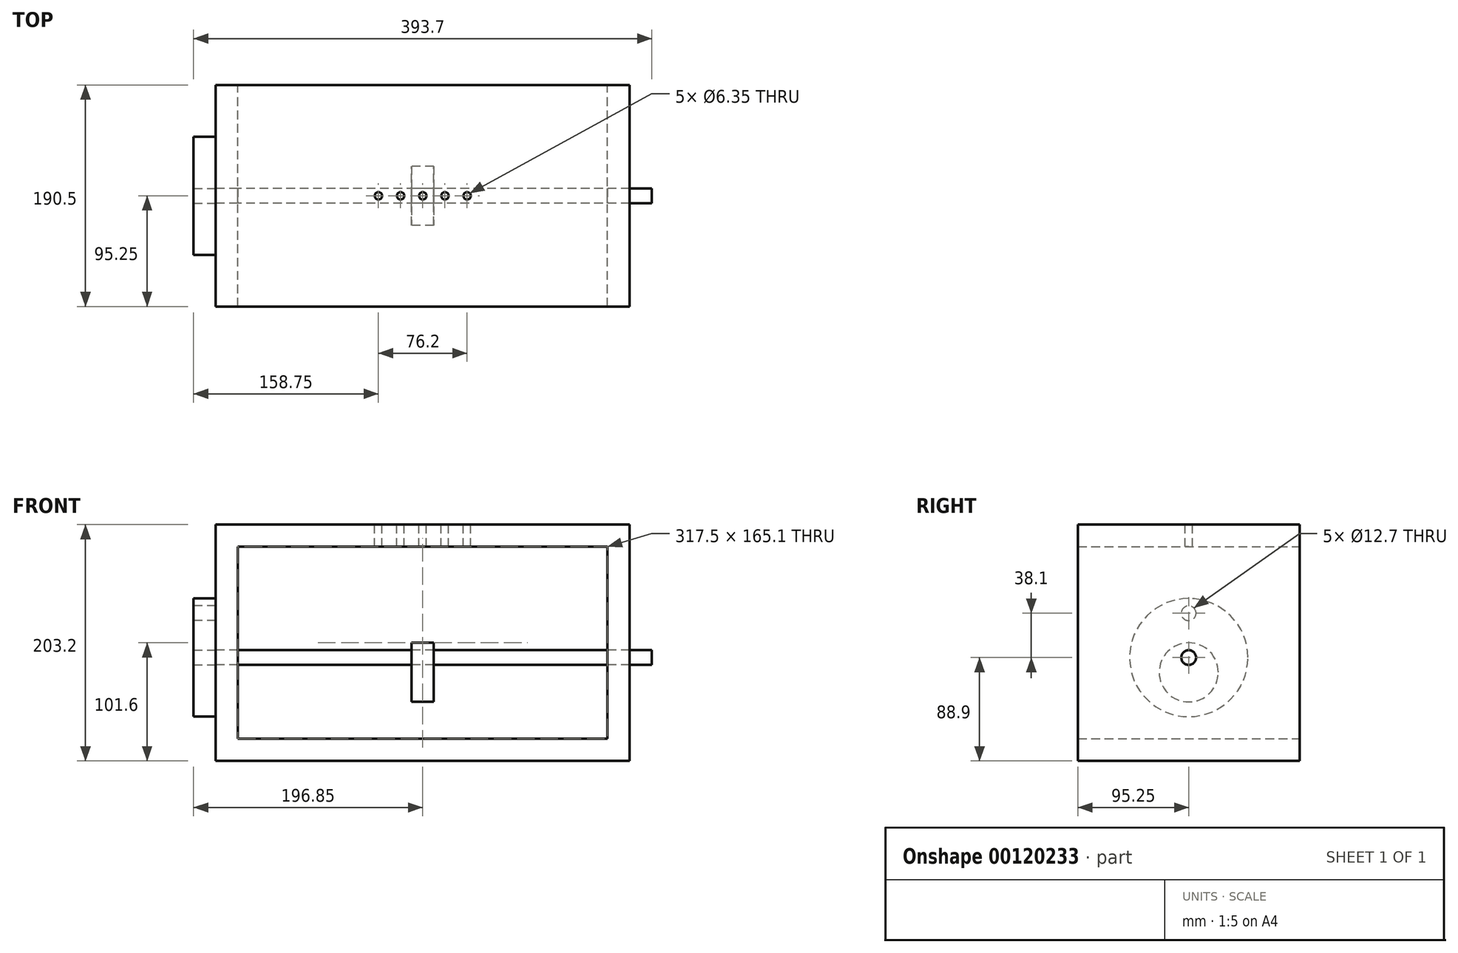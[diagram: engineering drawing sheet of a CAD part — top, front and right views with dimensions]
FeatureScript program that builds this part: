
annotation { "Feature Type Name" : "Feature", "Feature Type Description" : "" }
export const myFeature = defineFeature(function(context is Context, id is Id, definition is map)
    precondition{}
    {
        {
            var Q0;
            Q0=qCreatedBy(makeId("Front.planeOp"),FACE);
            var sketch = newSketch(context, id + "F0", { "sketchPlane" : qUnion([Q0])});
            skLineSegment(sketch, "E0.bottom", {"start": v(158.75, -82.55) * mm, "end": v(-158.75, -82.55) * mm});
            skLineSegment(sketch, "E0.top", {"start": v(158.75, 82.55) * mm, "end": v(-158.75, 82.55) * mm});
            skLineSegment(sketch, "E0.left", {"start": v(158.75, -82.55) * mm, "end": v(158.75, 82.55) * mm});
            skLineSegment(sketch, "E0.right", {"start": v(-158.75, -82.55) * mm, "end": v(-158.75, 82.55) * mm});
            skPoint(sketch, "E0.middle", {"position": v(0, 0) * mm});
            skLineSegment(sketch, "E1.bottom", {"start": v(177.8, -101.6) * mm, "end": v(-177.8, -101.6) * mm});
            skLineSegment(sketch, "E1.top", {"start": v(177.8, 101.6) * mm, "end": v(-177.8, 101.6) * mm});
            skLineSegment(sketch, "E1.left", {"start": v(177.8, -101.6) * mm, "end": v(177.8, 101.6) * mm});
            skLineSegment(sketch, "E1.right", {"start": v(-177.8, -101.6) * mm, "end": v(-177.8, 101.6) * mm});
            skSolve(sketch);
        }
        {
            var Q0;
            Q0=qSketchRegion(id+"F0",true);
            extrude(context, id + "F1", {"entities" : qUnion([Q0]), "endBound" : BoundingType.SYMMETRIC, "depth" : 190.5 * mm});
        }
        {
            var Q0;
            Q0=makeQuery(id+"F1.opExtrude","SWEPT_FACE",FACE,{"disambiguationData":[OSD([sQuery(id+"F0.wireOp",EDGE,"E1.right")])]});
            var sketch = newSketch(context, id + "F2", { "sketchPlane" : qUnion([Q0])});
            skCircle(sketch, "E2", {"center": v(0, -12.7) * mm, "radius": 6.35 * mm});
            skSolve(sketch);
        }
        {
            var Q0;
            Q0=qSketchRegion(id+"F2",true);
            extrude(context, id + "F3", {"entities" : qUnion([Q0]), "operationType" : NewBodyOperationType.REMOVE, "endBound" : BoundingType.THROUGH_ALL, "oppositeDirection" : true, "depth" : 25.4 * mm});
        }
        {
            var Q0;
            Q0=makeQuery(id+"F1.opExtrude","SWEPT_FACE",FACE,{"disambiguationData":[OSD([sQuery(id+"F0.wireOp",EDGE,"E1.right")])]});
            var sketch = newSketch(context, id + "F4", { "sketchPlane" : qUnion([Q0])});
            skCircle(sketch, "E3", {"center": v(0, -12.7) * mm, "radius": 50.8 * mm});
            skCircle(sketch, "E4.0", {"center": v(0, -12.7) * mm, "radius": 6.35 * mm});
            skSolve(sketch);
        }
        {
            var Q0;
            Q0=qSketchRegion(id+"F4",true);
            extrude(context, id + "F5", {"entities" : qUnion([Q0]), "depth" : 19.05 * mm});
        }
        {
            var Q0;
            Q0=makeQuery(id+"F5.opExtrude","CAP_FACE",FACE,{"disambiguationData":[OSD([sQuery(id+"F4.wireOp",EDGE,"E3"),sQuery(id+"F4.wireOp",EDGE,"E4.0")])],"isStart":false});
            var sketch = newSketch(context, id + "F6", { "sketchPlane" : qUnion([Q0])});
            skCircle(sketch, "E5", {"center": v(0, 25.4) * mm, "radius": 6.35 * mm});
            skLineSegment(sketch, "E6", {"start": v(0, -12.7) * mm, "end": v(0, 25.4) * mm, "construction": true});
            skSolve(sketch);
        }
        {
            var Q0;
            Q0=qSketchRegion(id+"F6",true);
            var Q1;
            Q1=makeQuery(id+"F1.opExtrude","SWEPT_FACE",FACE,{"disambiguationData":[OSD([sQuery(id+"F0.wireOp",EDGE,"E1.right")])]});
            extrude(context, id + "F7", {"entities" : qUnion([Q0]), "operationType" : NewBodyOperationType.REMOVE, "endBound" : BoundingType.UP_TO_SURFACE, "oppositeDirection" : true, "endBoundEntityFace" : qUnion([Q1]), "depth" : 25.4 * mm});
        }
        {
            var Q0;
            Q0=sQuery(id+"F6.wireOp",EDGE,"E5");
            extrude(context, id + "F8", {"bodyType" : ToolBodyType.SURFACE, "surfaceEntities" : qUnion([Q0]), "depth" : 114.3 * mm});
        }
        {
            var Q0;
            Q0=makeQuery(id+"F1.opExtrude","SWEPT_FACE",FACE,{"disambiguationData":[OSD([sQuery(id+"F0.wireOp",EDGE,"E0.right")])]});
            var sketch = newSketch(context, id + "F9", { "sketchPlane" : qUnion([Q0])});
            skCircle(sketch, "E7.0", {"center": v(0, -12.7) * mm, "radius": 6.35 * mm});
            skSolve(sketch);
        }
        {
            var Q0;
            Q0=qSketchRegion(id+"F9",true);
            extrude(context, id + "F10", {"entities" : qUnion([Q0]), "depth" : 355.6 * mm});
        }
        {
            var Q0;
            Q0=qCreatedBy(makeId("Right.planeOp"),FACE);
            var sketch = newSketch(context, id + "F11", { "sketchPlane" : qUnion([Q0])});
            skCircle(sketch, "E8.0", {"center": v(0, -12.7) * mm, "radius": 6.35 * mm});
            skCircle(sketch, "E9", {"center": v(0, -25.4) * mm, "radius": 25.4 * mm});
            skLineSegment(sketch, "E10", {"start": v(0, -12.7) * mm, "end": v(0, 0) * mm, "construction": true});
            skSolve(sketch);
        }
        {
            var Q0;
            Q0 = qSketchRegion(id + "F11", true);
            extrude(context, id + "F12", {"entities" : qUnion([Q0]), "endBound" : BoundingType.SYMMETRIC, "depth" : 19.05 * mm});
        }
        {
            var Q0;
            Q0=makeQuery(id+"F1.opExtrude","SWEPT_FACE",FACE,{"disambiguationData":[OSD([sQuery(id+"F0.wireOp",EDGE,"E1.top")])]});
            var sketch = newSketch(context, id + "F13", { "sketchPlane" : qUnion([Q0])});
            skLineSegment(sketch, "E11", {"start": v(0, 0) * mm, "end": v(19.05, 0) * mm, "construction": true});
            skLineSegment(sketch, "E12", {"start": v(19.05, 0) * mm, "end": v(38.1, 0) * mm, "construction": true});
            skLineSegment(sketch, "E13", {"start": v(0, 0) * mm, "end": v(-19.05, 0) * mm, "construction": true});
            skLineSegment(sketch, "E14", {"start": v(-19.05, 0) * mm, "end": v(-38.1, 0) * mm, "construction": true});
            skCircle(sketch, "E15", {"center": v(-38.1, 0) * mm, "radius": 3.18 * mm});
            skCircle(sketch, "E16", {"center": v(-19.05, 0) * mm, "radius": 3.18 * mm});
            skCircle(sketch, "E17", {"center": v(0, 0) * mm, "radius": 3.18 * mm});
            skCircle(sketch, "E18", {"center": v(19.05, 0) * mm, "radius": 3.18 * mm});
            skCircle(sketch, "E19", {"center": v(38.1, 0) * mm, "radius": 3.18 * mm});
            skSolve(sketch);
        }
        {
            var Q0;
            Q0 = qSketchRegion(id + "F13", true);
            var Q1;
            Q1=makeQuery(id+"F1.opExtrude","SWEPT_FACE",FACE,{"disambiguationData":[OSD([sQuery(id+"F0.wireOp",EDGE,"E0.top")])]});
            extrude(context, id + "F14", {"entities" : qUnion([Q0]), "operationType" : NewBodyOperationType.REMOVE, "endBound" : BoundingType.UP_TO_SURFACE, "oppositeDirection" : true, "endBoundEntityFace" : qUnion([Q1]), "depth" : 25.4 * mm});
        }
    });
